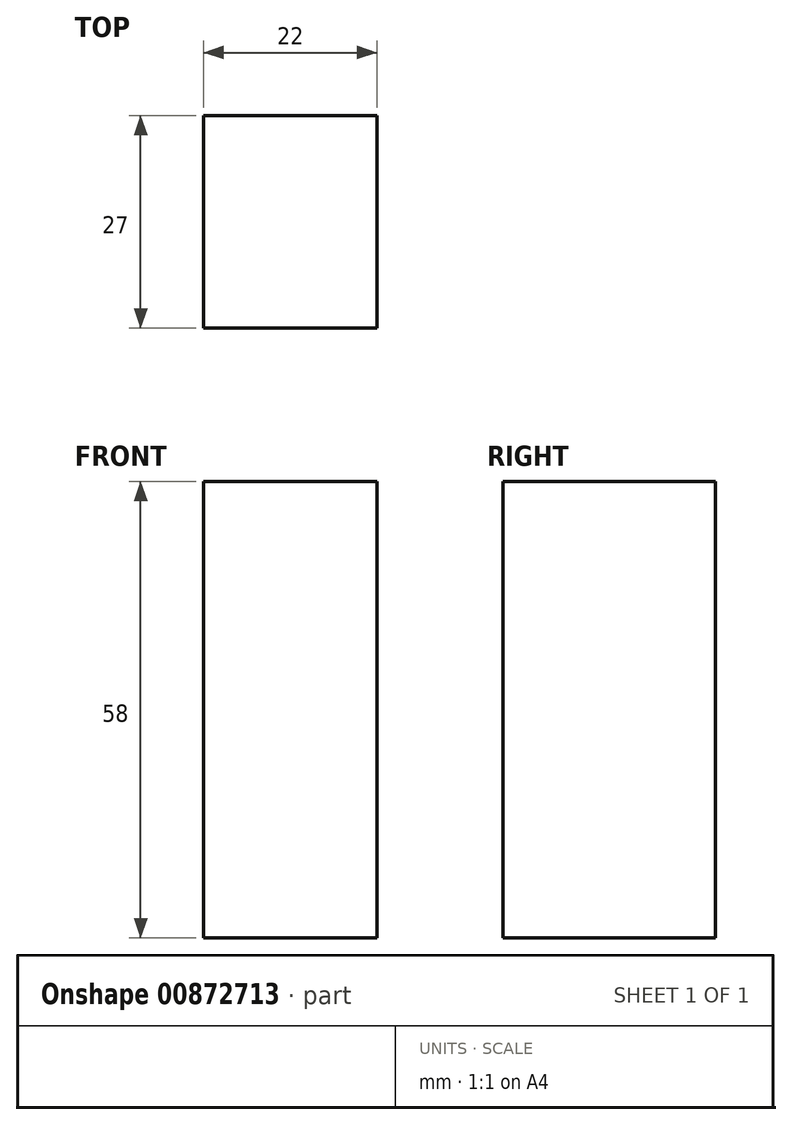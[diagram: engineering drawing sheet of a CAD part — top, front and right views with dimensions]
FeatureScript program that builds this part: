
annotation { "Feature Type Name" : "Feature", "Feature Type Description" : "" }
export const myFeature = defineFeature(function(context is Context, id is Id, definition is map)
    precondition{}
    {
        {
            var Q0;
            Q0=qCreatedBy(makeId("Top.planeOp"),FACE);
            var sketch = newSketch(context, id + "F0", { "sketchPlane" : qUnion([Q0])});
            skLineSegment(sketch, "E0.bottom", {"start": v(11, 13.5) * mm, "end": v(-11, 13.5) * mm});
            skLineSegment(sketch, "E0.top", {"start": v(11, -13.5) * mm, "end": v(-11, -13.5) * mm});
            skLineSegment(sketch, "E0.left", {"start": v(11, 13.5) * mm, "end": v(11, -13.5) * mm});
            skLineSegment(sketch, "E0.right", {"start": v(-11, 13.5) * mm, "end": v(-11, -13.5) * mm});
            skPoint(sketch, "E0.middle", {"position": v(0, 0) * mm});
            skSolve(sketch);
        }
        {
            var Q0;
            Q0=makeQuery(id+"F0.imprint","IMPRINT",FACE,{"disambiguationData":[TD([[makeQuery(id+"F0.imprint","IMPRINT",EDGE,{"derivedFrom":sQuery(id+"F0.wireOp",EDGE,"E0.bottom")}),1.0]])]});
            extrude(context, id + "F1", {"entities" : qUnion([Q0]), "depth" : 58 * mm, "offsetDistance" : 25.4 * mm});
        }
    });
